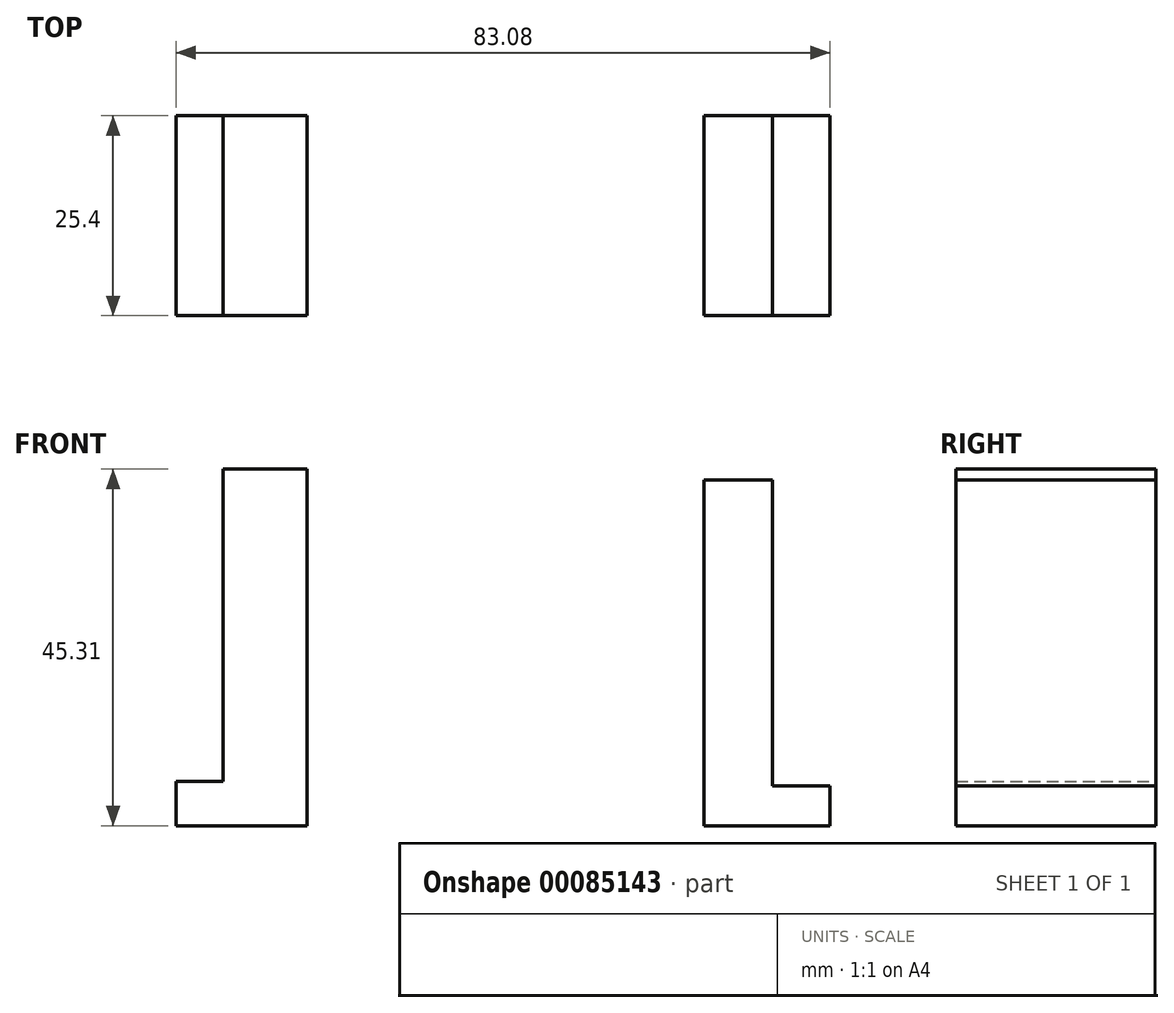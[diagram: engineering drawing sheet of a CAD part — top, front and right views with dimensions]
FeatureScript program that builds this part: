
annotation { "Feature Type Name" : "Feature", "Feature Type Description" : "" }
export const myFeature = defineFeature(function(context is Context, id is Id, definition is map)
    precondition{}
    {
        {
            var Q0;
            Q0=qCreatedBy(makeId("Front.planeOp"),FACE);
            var sketch = newSketch(context, id + "F0", { "sketchPlane" : qUnion([Q0])});
            skLineSegment(sketch, "E0.bottom", {"start": v(-50.96, 45.3) * mm, "end": v(-40.25, 45.3) * mm});
            skLineSegment(sketch, "E0.top", {"start": v(-50.96, 5.65) * mm, "end": v(-40.25, 5.65) * mm});
            skLineSegment(sketch, "E0.left", {"start": v(-50.96, 45.3) * mm, "end": v(-50.96, 5.65) * mm});
            skLineSegment(sketch, "E0.right", {"start": v(-40.25, 45.3) * mm, "end": v(-40.25, 5.65) * mm});
            skLineSegment(sketch, "E1.bottom", {"start": v(10.11, 43.92) * mm, "end": v(18.84, 43.92) * mm});
            skLineSegment(sketch, "E1.top", {"start": v(10.11, 5.06) * mm, "end": v(18.84, 5.06) * mm});
            skLineSegment(sketch, "E1.left", {"start": v(10.11, 43.92) * mm, "end": v(10.11, 5.06) * mm});
            skLineSegment(sketch, "E1.right", {"start": v(18.84, 43.92) * mm, "end": v(18.84, 5.06) * mm});
            skLineSegment(sketch, "E2.bottom", {"start": v(-40.25, 5.65) * mm, "end": v(-56.9, 5.65) * mm});
            skLineSegment(sketch, "E2.top", {"start": v(-40.25, 0) * mm, "end": v(-56.9, 0) * mm});
            skLineSegment(sketch, "E2.left", {"start": v(-40.25, 5.65) * mm, "end": v(-40.25, 0) * mm});
            skLineSegment(sketch, "E2.right", {"start": v(-56.9, 5.65) * mm, "end": v(-56.9, 0) * mm});
            skLineSegment(sketch, "E3.bottom", {"start": v(10.11, 5.06) * mm, "end": v(26.17, 5.06) * mm});
            skLineSegment(sketch, "E3.top", {"start": v(10.11, 0) * mm, "end": v(26.17, 0) * mm});
            skLineSegment(sketch, "E3.left", {"start": v(10.11, 5.06) * mm, "end": v(10.11, 0) * mm});
            skLineSegment(sketch, "E3.right", {"start": v(26.17, 5.06) * mm, "end": v(26.17, 0) * mm});
            skSolve(sketch);
        }
        {
            var Q0;
            Q0=makeQuery(id+"F0.imprint","IMPRINT",FACE,{"disambiguationData":[TD([[makeQuery(id+"F0.imprint","IMPRINT",EDGE,{"derivedFrom":sQuery(id+"F0.wireOp",EDGE,"E0.bottom")}),-1.0]])]});
            var Q1;
            Q1=makeQuery(id+"F0.imprint","IMPRINT",FACE,{"disambiguationData":[TD([[makeQuery(id+"F0.imprint","IMPRINT",EDGE,{"derivedFrom":sQuery(id+"F0.wireOp",EDGE,"E2.top")}),-1.0]])]});
            var Q2;
            Q2=makeQuery(id+"F0.imprint","IMPRINT",FACE,{"disambiguationData":[TD([[makeQuery(id+"F0.imprint","IMPRINT",EDGE,{"derivedFrom":sQuery(id+"F0.wireOp",EDGE,"E1.bottom")}),-1.0]])]});
            var Q3;
            Q3=makeQuery(id+"F0.imprint","IMPRINT",FACE,{"disambiguationData":[TD([[makeQuery(id+"F0.imprint","IMPRINT",EDGE,{"derivedFrom":sQuery(id+"F0.wireOp",EDGE,"E3.top")}),1.0]])]});
            extrude(context, id + "F1", {"entities" : qUnion([Q0, Q1, Q2, Q3]), "depth" : 25.4 * mm});
        }
    });
